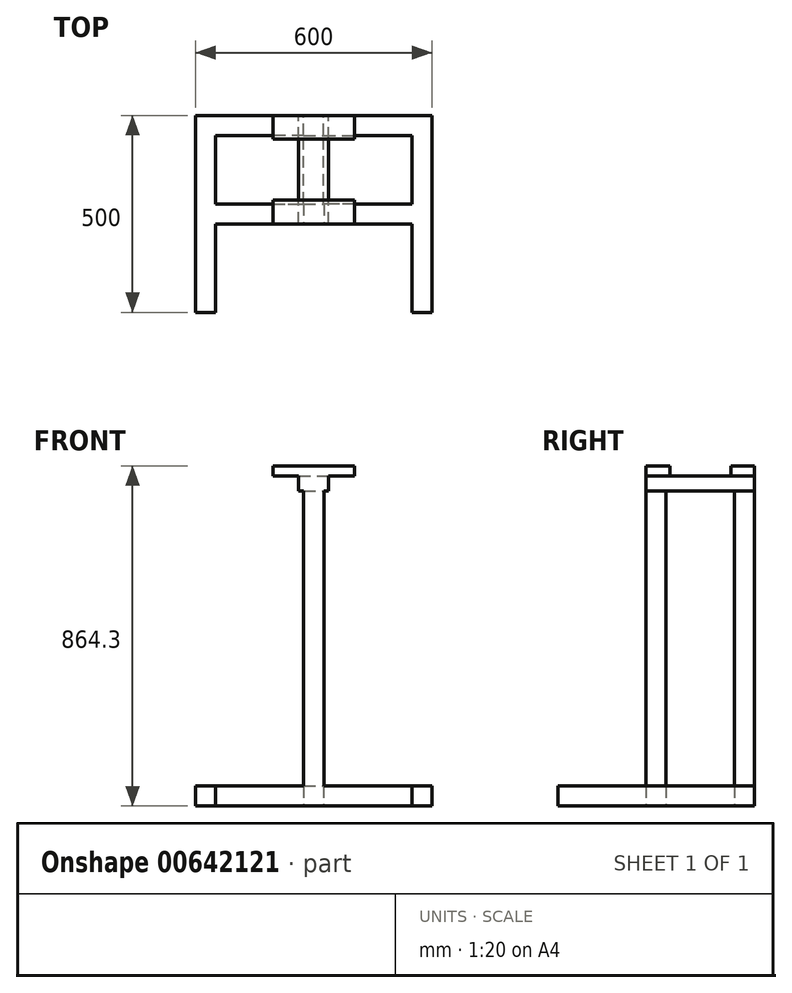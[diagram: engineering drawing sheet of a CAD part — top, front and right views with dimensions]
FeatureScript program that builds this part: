
annotation { "Feature Type Name" : "Feature", "Feature Type Description" : "" }
export const myFeature = defineFeature(function(context is Context, id is Id, definition is map)
    precondition{}
    {
        {
            var Q0;
            Q0=qCreatedBy(makeId("Top.planeOp"),FACE);
            var sketch = newSketch(context, id + "F0", { "sketchPlane" : qUnion([Q0])});
            skLineSegment(sketch, "E0.left", {"start": v(-300, 250) * mm, "end": v(-300, -250) * mm});
            skPoint(sketch, "E0.middle", {"position": v(0, 0) * mm});
            skLineSegment(sketch, "E1", {"start": v(-249.2, -250) * mm, "end": v(-249.2, -25.4) * mm});
            skLineSegment(sketch, "E2", {"start": v(-249.2, -25.4) * mm, "end": v(0, -25.4) * mm});
            skLineSegment(sketch, "E3", {"start": v(-249.2, 25.4) * mm, "end": v(-25.4, 25.4) * mm});
            skLineSegment(sketch, "E4", {"start": v(-25.4, 25.4) * mm, "end": v(-25.4, 199.2) * mm});
            skLineSegment(sketch, "E5", {"start": v(-25.4, 199.2) * mm, "end": v(-249.2, 199.2) * mm});
            skLineSegment(sketch, "E6", {"start": v(-249.2, 199.2) * mm, "end": v(-249.2, 25.4) * mm});
            skLineSegment(sketch, "E7", {"start": v(-300, -250) * mm, "end": v(-249.2, -250) * mm});
            skLineSegment(sketch, "E8", {"start": v(-300, 250) * mm, "end": v(0, 250) * mm});
            skLineSegment(sketch, "E9.MirrorCS", {"start": v(300, 250) * mm, "end": v(0, 250) * mm});
            skLineSegment(sketch, "E10.MirrorCS", {"start": v(25.4, 199.2) * mm, "end": v(249.2, 199.2) * mm});
            skLineSegment(sketch, "E11.MirrorCS", {"start": v(25.4, 25.4) * mm, "end": v(25.4, 199.2) * mm});
            skLineSegment(sketch, "E12.MirrorCS", {"start": v(249.2, 25.4) * mm, "end": v(25.4, 25.4) * mm});
            skLineSegment(sketch, "E13.MirrorCS", {"start": v(249.2, 199.2) * mm, "end": v(249.2, 25.4) * mm});
            skLineSegment(sketch, "E14.MirrorCS", {"start": v(300, 250) * mm, "end": v(300, -250) * mm});
            skLineSegment(sketch, "E15.MirrorCS", {"start": v(249.2, -250) * mm, "end": v(249.2, -25.4) * mm});
            skLineSegment(sketch, "E16.MirrorCS", {"start": v(249.2, -25.4) * mm, "end": v(0, -25.4) * mm});
            skLineSegment(sketch, "E17.MirrorCS", {"start": v(300, -250) * mm, "end": v(249.2, -250) * mm});
            skSolve(sketch);
        }
        {
            var Q0;
            Q0 = qSketchRegion(id + "F0", true);
            extrude(context, id + "F1", {"entities" : qUnion([Q0]), "depth" : 50.8 * mm, "offsetDistance" : 25 * mm});
        }
        {
            var Q0;
            Q0=makeQuery(id+"F1.opExtrude","CAP_FACE",FACE,{"disambiguationData":[OSD([sQuery(id+"F0.wireOp",EDGE,"E0.left"),sQuery(id+"F0.wireOp",EDGE,"E1"),sQuery(id+"F0.wireOp",EDGE,"E2"),sQuery(id+"F0.wireOp",EDGE,"E3"),sQuery(id+"F0.wireOp",EDGE,"E4"),sQuery(id+"F0.wireOp",EDGE,"E5"),sQuery(id+"F0.wireOp",EDGE,"E6"),sQuery(id+"F0.wireOp",EDGE,"E7"),sQuery(id+"F0.wireOp",EDGE,"E8"),sQuery(id+"F0.wireOp",EDGE,"E9.MirrorCS"),sQuery(id+"F0.wireOp",EDGE,"E10.MirrorCS"),sQuery(id+"F0.wireOp",EDGE,"E11.MirrorCS"),sQuery(id+"F0.wireOp",EDGE,"E12.MirrorCS"),sQuery(id+"F0.wireOp",EDGE,"E13.MirrorCS"),sQuery(id+"F0.wireOp",EDGE,"E14.MirrorCS"),sQuery(id+"F0.wireOp",EDGE,"E15.MirrorCS"),sQuery(id+"F0.wireOp",EDGE,"E16.MirrorCS"),sQuery(id+"F0.wireOp",EDGE,"E17.MirrorCS")])],"isStart":false});
            var sketch = newSketch(context, id + "F2", { "sketchPlane" : qUnion([Q0])});
            skLineSegment(sketch, "E18.bottom", {"start": v(-25.4, 25.4) * mm, "end": v(25.83, 25.4) * mm});
            skLineSegment(sketch, "E18.top", {"start": v(-25.4, -25.4) * mm, "end": v(25.83, -25.4) * mm});
            skLineSegment(sketch, "E18.left", {"start": v(-25.4, 25.4) * mm, "end": v(-25.4, -25.4) * mm});
            skLineSegment(sketch, "E18.right", {"start": v(25.83, 25.4) * mm, "end": v(25.83, -25.4) * mm});
            skLineSegment(sketch, "E19.bottom", {"start": v(-25.4, 199.2) * mm, "end": v(25.4, 199.2) * mm});
            skLineSegment(sketch, "E19.top", {"start": v(-25.4, 250) * mm, "end": v(25.4, 250) * mm});
            skLineSegment(sketch, "E19.left", {"start": v(-25.4, 199.2) * mm, "end": v(-25.4, 250) * mm});
            skLineSegment(sketch, "E19.right", {"start": v(25.4, 199.2) * mm, "end": v(25.4, 250) * mm});
            skSolve(sketch);
        }
        {
            var Q0;
            Q0 = qSketchRegion(id + "F2", true);
            extrude(context, id + "F3", {"entities" : qUnion([Q0]), "operationType" : NewBodyOperationType.ADD, "depth" : 750 * mm, "offsetDistance" : 25 * mm});
        }
        {
            var Q0;
            Q0=qCreatedBy(makeId("Top.planeOp"),FACE);
            cPlane(context, id + "F4", {"entities" : qUnion([Q0]), "cplaneType" : CPlaneType.OFFSET, "offset" : 800.8 * mm, "width" : 150 * mm, "height" : 150 * mm});
        }
        {
            var Q0;
            Q0=qCreatedBy(id+"F4.planeOp",FACE);
            var sketch = newSketch(context, id + "F5", { "sketchPlane" : qUnion([Q0])});
            skLineSegment(sketch, "E20.bottom", {"start": v(38.1, -25.4) * mm, "end": v(-38.1, -25.4) * mm});
            skLineSegment(sketch, "E20.top", {"start": v(38.1, 250) * mm, "end": v(-38.1, 250) * mm});
            skLineSegment(sketch, "E20.left", {"start": v(38.1, -25.4) * mm, "end": v(38.1, 250) * mm});
            skLineSegment(sketch, "E20.right", {"start": v(-38.1, -25.4) * mm, "end": v(-38.1, 250) * mm});
            skSolve(sketch);
        }
        {
            var Q0;
            Q0 = qSketchRegion(id + "F5", true);
            extrude(context, id + "F6", {"entities" : qUnion([Q0]), "operationType" : NewBodyOperationType.ADD, "depth" : 38.1 * mm, "offsetDistance" : 25 * mm});
        }
        {
            var Q0;
            Q0=qCreatedBy(id+"F4.planeOp",FACE);
            cPlane(context, id + "F7", {"entities" : qUnion([Q0]), "cplaneType" : CPlaneType.OFFSET, "offset" : 38.1 * mm, "width" : 150 * mm, "height" : 150 * mm});
        }
        {
            var Q0;
            Q0=qCreatedBy(id+"F7.planeOp",FACE);
            var sketch = newSketch(context, id + "F8", { "sketchPlane" : qUnion([Q0])});
            skPoint(sketch, "E21.middle", {"position": v(0, 0) * mm});
            skPoint(sketch, "E22", {"position": v(-38.1, -25.4) * mm});
            skLineSegment(sketch, "E23", {"start": v(103, -25.4) * mm, "end": v(103, 34.6) * mm});
            skLineSegment(sketch, "E24", {"start": v(103, 34.6) * mm, "end": v(-103, 34.6) * mm});
            skLineSegment(sketch, "E25", {"start": v(-103, 34.6) * mm, "end": v(-103, -25.4) * mm});
            skLineSegment(sketch, "E26", {"start": v(-103, -25.4) * mm, "end": v(103, -25.4) * mm});
            skLineSegment(sketch, "E27", {"start": v(103, 190) * mm, "end": v(103, 250) * mm});
            skLineSegment(sketch, "E28", {"start": v(103, 250) * mm, "end": v(-103, 250) * mm});
            skLineSegment(sketch, "E29", {"start": v(-103, 250) * mm, "end": v(-103, 190) * mm});
            skLineSegment(sketch, "E30", {"start": v(-103, 190) * mm, "end": v(103, 190) * mm});
            skSolve(sketch);
        }
        {
            var Q0;
            Q0 = qSketchRegion(id + "F8", true);
            extrude(context, id + "F9", {"entities" : qUnion([Q0]), "operationType" : NewBodyOperationType.ADD, "depth" : 25.4 * mm, "offsetDistance" : 25 * mm});
        }
    });
